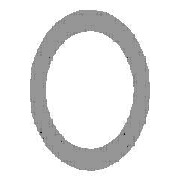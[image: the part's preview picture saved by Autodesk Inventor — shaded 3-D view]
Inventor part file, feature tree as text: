
AUTODESK INVENTOR PART (.ipt)
format: ipt  version: 2013 (Build 170138000, 138)  size: 112,640 bytes
history: native  units: mm (DEFAULTED — no unit token found)
features: other x4, sketch x3, plane x2
ambient origin geometry x8: Origin, YZ Plane, XZ Plane, XY Plane, X Axis, Y Axis, Z Axis, Center Point
bodies: Solid1 (feature_tree), Body (feature_tree)
feature tree (9):
  parser-record x1  (decoder bookkeeping rows leaked as tree rows — omitted from the tree; the rows remain in map.json)
  other  "Driven Length"
  other  "Start plane"
  other  "End plane"
  plane  "Work Plane4"
  sketch  "Sketch"  dims[d2=1727.2mm d3=0.0mm d4=-0.0mm d5=1727.2mm d6=90.0deg d7=1727.2mm]
  sketch  "Sketch3"  dims[d0=42.164mm]
  plane  "Work Plane3"
  sketch  "Sketch4"  dims[d1=3.556mm]
